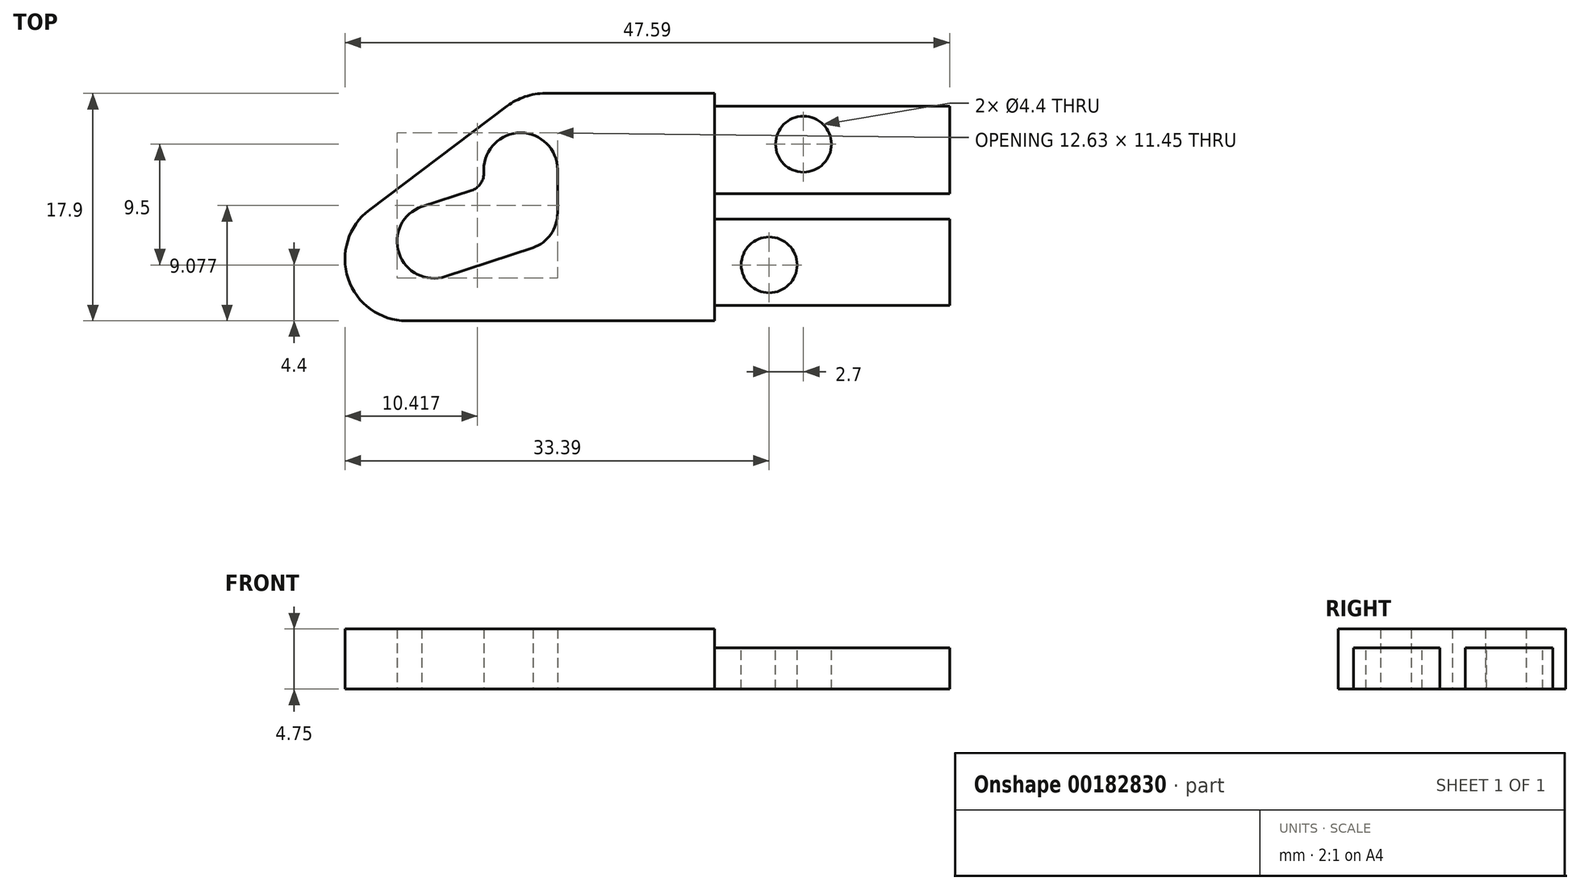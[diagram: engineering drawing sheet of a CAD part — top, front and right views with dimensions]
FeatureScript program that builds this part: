
annotation { "Feature Type Name" : "Feature", "Feature Type Description" : "" }
export const myFeature = defineFeature(function(context is Context, id is Id, definition is map)
    precondition{}
    {
        {
            var Q0;
            Q0=qCreatedBy(makeId("Top.planeOp"),FACE);
            var sketch = newSketch(context, id + "F0", { "sketchPlane" : qUnion([Q0])});
            skLineSegment(sketch, "E0", {"start": v(-29.7, 19.73) * mm, "end": v(-14.7, 19.73) * mm});
            skLineSegment(sketch, "E1", {"start": v(-14.7, 19.73) * mm, "end": v(-14.7, 18.73) * mm});
            skLineSegment(sketch, "E2", {"start": v(-14.7, 18.73) * mm, "end": v(3.8, 18.73) * mm});
            skLineSegment(sketch, "E3", {"start": v(3.8, 18.73) * mm, "end": v(3.8, 11.83) * mm});
            skLineSegment(sketch, "E4", {"start": v(3.8, 11.83) * mm, "end": v(-14.7, 11.83) * mm});
            skLineSegment(sketch, "E5", {"start": v(-14.7, 11.83) * mm, "end": v(-14.7, 9.83) * mm});
            skLineSegment(sketch, "E6", {"start": v(-14.7, 9.83) * mm, "end": v(3.8, 9.83) * mm});
            skLineSegment(sketch, "E7", {"start": v(3.8, 9.83) * mm, "end": v(3.8, 3.03) * mm});
            skLineSegment(sketch, "E8", {"start": v(3.8, 3.03) * mm, "end": v(-14.7, 3.03) * mm});
            skLineSegment(sketch, "E9", {"start": v(-14.7, 3.03) * mm, "end": v(-14.7, 1.83) * mm});
            skLineSegment(sketch, "E10", {"start": v(-14.7, 1.83) * mm, "end": v(-38.94, 1.83) * mm});
            skLineSegment(sketch, "E11", {"start": v(-43.8, 9.1) * mm, "end": v(-43.8, 1.83) * mm});
            skLineSegment(sketch, "E12", {"start": v(-29.7, 19.73) * mm, "end": v(-41.86, 10.56) * mm});
            skArc(sketch, "E13", {"start": v(-41.86, 10.56) * mm, "mid": v(-43.54, 5.14) * mm, "end": v(-38.94, 1.83) * mm});
            skLineSegment(sketch, "E14.0", {"start": v(-43.75, 9.1) * mm, "end": v(-43.75, 1.83) * mm});
            skLineSegment(sketch, "E15.0", {"start": v(-37.74, 10.82) * mm, "end": v(-33.83, 12.09) * mm});
            skLineSegment(sketch, "E16.0", {"start": v(-35.89, 5.32) * mm, "end": v(-29, 7.58) * mm});
            skLineSegment(sketch, "E17.0", {"start": v(-27.06, 13.73) * mm, "end": v(-27.06, 10.33) * mm});
            skArc(sketch, "E18", {"start": v(-27.06, 10.33) * mm, "mid": v(-27.59, 8.64) * mm, "end": v(-29, 7.58) * mm});
            skArc(sketch, "E19", {"start": v(-33.83, 12.09) * mm, "mid": v(-33.13, 12.6) * mm, "end": v(-32.86, 13.41) * mm});
            skArc(sketch, "E20", {"start": v(-27.06, 13.73) * mm, "mid": v(-29.96, 16.63) * mm, "end": v(-32.86, 13.73) * mm});
            skArc(sketch, "E21", {"start": v(-37.74, 10.82) * mm, "mid": v(-39.54, 7.15) * mm, "end": v(-35.89, 5.32) * mm});
            skLineSegment(sketch, "E22", {"start": v(-32.86, 13.73) * mm, "end": v(-32.86, 13.41) * mm});
            skLineSegment(sketch, "E23", {"start": v(-14.7, 18.73) * mm, "end": v(-14.7, 11.83) * mm});
            skLineSegment(sketch, "E24", {"start": v(-14.7, 9.83) * mm, "end": v(-14.7, 3.03) * mm});
            skLineSegment(sketch, "E25.top", {"start": v(-14.7, 11.83) * mm, "end": v(3.8, 11.83) * mm});
            skLineSegment(sketch, "E26.top", {"start": v(-14.7, 3.03) * mm, "end": v(3.8, 3.03) * mm});
            skSolve(sketch);
        }
        {
            var Q0;
            Q0 = qSketchRegion(id + "F0", true);
            extrude(context, id + "F1", {"entities" : qUnion([Q0]), "depth" : 3.25 * mm});
        }
        {
            var Q0;
            Q0=makeQuery(id+"F1.opExtrude","CAP_FACE",FACE,{"disambiguationData":[OSD([sQuery(id+"F0.wireOp",EDGE,"E0"),sQuery(id+"F0.wireOp",EDGE,"E1"),sQuery(id+"F0.wireOp",EDGE,"E5"),sQuery(id+"F0.wireOp",EDGE,"E9"),sQuery(id+"F0.wireOp",EDGE,"E10"),sQuery(id+"F0.wireOp",EDGE,"E12"),sQuery(id+"F0.wireOp",EDGE,"E13"),sQuery(id+"F0.wireOp",EDGE,"E15.0"),sQuery(id+"F0.wireOp",EDGE,"E16.0"),sQuery(id+"F0.wireOp",EDGE,"E17.0"),sQuery(id+"F0.wireOp",EDGE,"E18"),sQuery(id+"F0.wireOp",EDGE,"E19"),sQuery(id+"F0.wireOp",EDGE,"E20"),sQuery(id+"F0.wireOp",EDGE,"E21"),sQuery(id+"F0.wireOp",EDGE,"E22"),sQuery(id+"F0.wireOp",EDGE,"Ak0rlIlP-qByR-QbEt-2pl7-ouNjJ3vkTCh7"),sQuery(id+"F0.wireOp",EDGE,"E2"),sQuery(id+"F0.wireOp",EDGE,"E25.top"),sQuery(id+"F0.wireOp",EDGE,"E3"),sQuery(id+"F0.wireOp",EDGE,"E6"),sQuery(id+"F0.wireOp",EDGE,"E26.top"),sQuery(id+"F0.wireOp",EDGE,"E7")])],"isStart":false});
            var sketch = newSketch(context, id + "F2", { "sketchPlane" : qUnion([Q0])});
            skLineSegment(sketch, "E27", {"start": v(-14.7, 19.73) * mm, "end": v(-14.7, 1.83) * mm});
            skSolve(sketch);
        }
        {
            var Q0;
            Q0 = qSketchRegion(id + "F2", true);
            var Q1;
            {var subQ2=makeQuery(id+"F1.opExtrude","CAP_EDGE",EDGE,{"disambiguationData":[OSD([sQuery(id+"F0.wireOp",EDGE,"E0")])],"isStart":false});Q1=makeQuery(id+"F2.imprint","IMPRINT",FACE,{"disambiguationData":[TD([[makeQuery(id+"F2.imprint","IMPRINT",EDGE,{"derivedFrom":subQ2}),-1.0]])]});}
            extrude(context, id + "F3", {"entities" : qUnion([Q0, Q1]), "operationType" : NewBodyOperationType.ADD, "depth" : 1.5 * mm});
        }
        {
            var Q0;
            {var subQ0=sQuery(id+"F0.wireOp",EDGE,"E12");var subQ1=sQuery(id+"F0.wireOp",EDGE,"E0");Q0=makeQuery(id+"F3.boolean.opBoolean","MERGE",EDGE,{"derivedFrom":[makeQuery(id+"F1.opExtrude","SWEPT_EDGE",EDGE,{"disambiguationData":[OSD([subQ1,subQ0])]}),makeQuery(id+"F3.opExtrude","SWEPT_EDGE",EDGE,{"disambiguationData":[OSD([subQ1,subQ0])]})]});}
            fillet(context, id + "F4", {"entities" : qUnion([Q0]), "radius" : 5 * mm, "tangentPropagation" : true, "allowEdgeOverflow" : false});
        }
        {
            var Q0;
            {var subQ0=sQuery(id+"F0.wireOp",EDGE,"E9");var subQ1=sQuery(id+"F0.wireOp",EDGE,"E5");var subQ2=sQuery(id+"F0.wireOp",EDGE,"E2");var subQ3=sQuery(id+"F0.wireOp",EDGE,"E1");var subQ4=sQuery(id+"F0.wireOp",EDGE,"E25.top");var subQ5=sQuery(id+"F0.wireOp",EDGE,"E3");Q0=makeQuery(id+"F3.boolean.opBoolean","SPLIT",FACE,{"disambiguationData":[TD([makeQuery(id+"F1.opExtrude","SWEPT_FACE",FACE,{"disambiguationData":[OSD([subQ2])]})])],"derivedFrom":makeQuery(id+"F1.opExtrude","CAP_FACE",FACE,{"disambiguationData":[OSD([sQuery(id+"F0.wireOp",EDGE,"E0"),subQ3,subQ1,subQ0,sQuery(id+"F0.wireOp",EDGE,"E10"),sQuery(id+"F0.wireOp",EDGE,"E12"),sQuery(id+"F0.wireOp",EDGE,"E13"),sQuery(id+"F0.wireOp",EDGE,"E15.0"),sQuery(id+"F0.wireOp",EDGE,"E16.0"),sQuery(id+"F0.wireOp",EDGE,"E17.0"),sQuery(id+"F0.wireOp",EDGE,"E18"),sQuery(id+"F0.wireOp",EDGE,"E19"),sQuery(id+"F0.wireOp",EDGE,"E20"),sQuery(id+"F0.wireOp",EDGE,"E21"),sQuery(id+"F0.wireOp",EDGE,"E22"),sQuery(id+"F0.wireOp",EDGE,"Ak0rlIlP-qByR-QbEt-2pl7-ouNjJ3vkTCh7"),subQ2,subQ4,subQ5,sQuery(id+"F0.wireOp",EDGE,"E6"),sQuery(id+"F0.wireOp",EDGE,"E26.top"),sQuery(id+"F0.wireOp",EDGE,"E7")])],"isStart":false})});}
            var sketch = newSketch(context, id + "F5", { "sketchPlane" : qUnion([Q0])});
            skLineSegment(sketch, "E28", {"start": v(-14.7, 18.73) * mm, "end": v(-14.7, 11.83) * mm});
            skLineSegment(sketch, "E29.0", {"start": v(-7.7, 18.73) * mm, "end": v(-7.7, 15.73) * mm});
            skLineSegment(sketch, "E30", {"start": v(-7.7, 18.73) * mm, "end": v(3.8, 18.73) * mm});
            skLineSegment(sketch, "E31.0", {"start": v(-14.7, 15.73) * mm, "end": v(-7.7, 15.73) * mm});
            skPoint(sketch, "E32", {"position": v(-6.91, 21.93) * mm});
            skPoint(sketch, "E33", {"position": v(-7.7, 15.73) * mm});
            skSolve(sketch);
        }
        {
            var Q0;
            Q0=sQuery(id+"F5.wireOp",VERTEX,"E33");
            var Q1;
            Q1=makeQuery(id+"F1.opExtrude","SWEPT_BODY",BODY,{"disambiguationData":[OSD([sQuery(id+"F0.wireOp",EDGE,"E0"),sQuery(id+"F0.wireOp",EDGE,"E1"),sQuery(id+"F0.wireOp",EDGE,"E5"),sQuery(id+"F0.wireOp",EDGE,"E9"),sQuery(id+"F0.wireOp",EDGE,"E10"),sQuery(id+"F0.wireOp",EDGE,"E12"),sQuery(id+"F0.wireOp",EDGE,"E13"),sQuery(id+"F0.wireOp",EDGE,"E15.0"),sQuery(id+"F0.wireOp",EDGE,"E16.0"),sQuery(id+"F0.wireOp",EDGE,"E17.0"),sQuery(id+"F0.wireOp",EDGE,"E18"),sQuery(id+"F0.wireOp",EDGE,"E19"),sQuery(id+"F0.wireOp",EDGE,"E20"),sQuery(id+"F0.wireOp",EDGE,"E21"),sQuery(id+"F0.wireOp",EDGE,"E22"),sQuery(id+"F0.wireOp",EDGE,"Ak0rlIlP-qByR-QbEt-2pl7-ouNjJ3vkTCh7"),sQuery(id+"F0.wireOp",EDGE,"E2"),sQuery(id+"F0.wireOp",EDGE,"E25.top"),sQuery(id+"F0.wireOp",EDGE,"E3"),sQuery(id+"F0.wireOp",EDGE,"E6"),sQuery(id+"F0.wireOp",EDGE,"E26.top"),sQuery(id+"F0.wireOp",EDGE,"E7")])]});
            hole(context, id + "F6", {"style" : HoleStyle.SIMPLE, "endStyle" : HoleEndStyle.THROUGH, "holeDiameter" : 4.4 * mm, "startFromSketch" : true, "locations" : qUnion([Q0]), "scope" : qUnion([Q1]), "isTappedThrough" : true});
        }
        {
            var Q0;
            {var subQ0=sQuery(id+"F0.wireOp",EDGE,"E6");var subQ1=sQuery(id+"F0.wireOp",EDGE,"E9");var subQ2=sQuery(id+"F0.wireOp",EDGE,"E5");var subQ3=sQuery(id+"F0.wireOp",EDGE,"E1");var subQ4=sQuery(id+"F0.wireOp",EDGE,"E26.top");var subQ5=sQuery(id+"F0.wireOp",EDGE,"E7");Q0=makeQuery(id+"F3.boolean.opBoolean","SPLIT",FACE,{"disambiguationData":[TD([makeQuery(id+"F1.opExtrude","SWEPT_FACE",FACE,{"disambiguationData":[OSD([subQ0])]})])],"derivedFrom":makeQuery(id+"F1.opExtrude","CAP_FACE",FACE,{"disambiguationData":[OSD([sQuery(id+"F0.wireOp",EDGE,"E0"),subQ3,subQ2,subQ1,sQuery(id+"F0.wireOp",EDGE,"E10"),sQuery(id+"F0.wireOp",EDGE,"E12"),sQuery(id+"F0.wireOp",EDGE,"E13"),sQuery(id+"F0.wireOp",EDGE,"E15.0"),sQuery(id+"F0.wireOp",EDGE,"E16.0"),sQuery(id+"F0.wireOp",EDGE,"E17.0"),sQuery(id+"F0.wireOp",EDGE,"E18"),sQuery(id+"F0.wireOp",EDGE,"E19"),sQuery(id+"F0.wireOp",EDGE,"E20"),sQuery(id+"F0.wireOp",EDGE,"E21"),sQuery(id+"F0.wireOp",EDGE,"E22"),sQuery(id+"F0.wireOp",EDGE,"Ak0rlIlP-qByR-QbEt-2pl7-ouNjJ3vkTCh7"),sQuery(id+"F0.wireOp",EDGE,"E2"),sQuery(id+"F0.wireOp",EDGE,"E25.top"),sQuery(id+"F0.wireOp",EDGE,"E3"),subQ0,subQ4,subQ5])],"isStart":false})});}
            var sketch = newSketch(context, id + "F7", { "sketchPlane" : qUnion([Q0])});
            skLineSegment(sketch, "E34", {"start": v(-14.7, 9.83) * mm, "end": v(-14.7, 3.03) * mm});
            skLineSegment(sketch, "E35", {"start": v(-14.7, 3.03) * mm, "end": v(3.8, 3.03) * mm});
            skLineSegment(sketch, "E36.0", {"start": v(-10.4, 7.33) * mm, "end": v(3.8, 7.33) * mm});
            skLineSegment(sketch, "E36.1", {"start": v(-10.4, 9.83) * mm, "end": v(-10.4, 6.23) * mm});
            skLineSegment(sketch, "E37.0", {"start": v(-10.4, 6.23) * mm, "end": v(3.8, 6.23) * mm});
            skPoint(sketch, "E38", {"position": v(-10.4, 6.23) * mm});
            skSolve(sketch);
        }
        {
            var Q0;
            Q0=sQuery(id+"F7.wireOp",VERTEX,"E38");
            var Q1;
            Q1=makeQuery(id+"F1.opExtrude","SWEPT_BODY",BODY,{"disambiguationData":[OSD([sQuery(id+"F0.wireOp",EDGE,"E0"),sQuery(id+"F0.wireOp",EDGE,"E1"),sQuery(id+"F0.wireOp",EDGE,"E5"),sQuery(id+"F0.wireOp",EDGE,"E9"),sQuery(id+"F0.wireOp",EDGE,"E10"),sQuery(id+"F0.wireOp",EDGE,"E12"),sQuery(id+"F0.wireOp",EDGE,"E13"),sQuery(id+"F0.wireOp",EDGE,"E15.0"),sQuery(id+"F0.wireOp",EDGE,"E16.0"),sQuery(id+"F0.wireOp",EDGE,"E17.0"),sQuery(id+"F0.wireOp",EDGE,"E18"),sQuery(id+"F0.wireOp",EDGE,"E19"),sQuery(id+"F0.wireOp",EDGE,"E20"),sQuery(id+"F0.wireOp",EDGE,"E21"),sQuery(id+"F0.wireOp",EDGE,"E22"),sQuery(id+"F0.wireOp",EDGE,"Ak0rlIlP-qByR-QbEt-2pl7-ouNjJ3vkTCh7"),sQuery(id+"F0.wireOp",EDGE,"E2"),sQuery(id+"F0.wireOp",EDGE,"E25.top"),sQuery(id+"F0.wireOp",EDGE,"E3"),sQuery(id+"F0.wireOp",EDGE,"E6"),sQuery(id+"F0.wireOp",EDGE,"E26.top"),sQuery(id+"F0.wireOp",EDGE,"E7")])]});
            hole(context, id + "F8", {"style" : HoleStyle.SIMPLE, "endStyle" : HoleEndStyle.THROUGH, "holeDiameter" : 4.4 * mm, "startFromSketch" : true, "locations" : qUnion([Q0]), "scope" : qUnion([Q1]), "isTappedThrough" : true});
        }
    });
